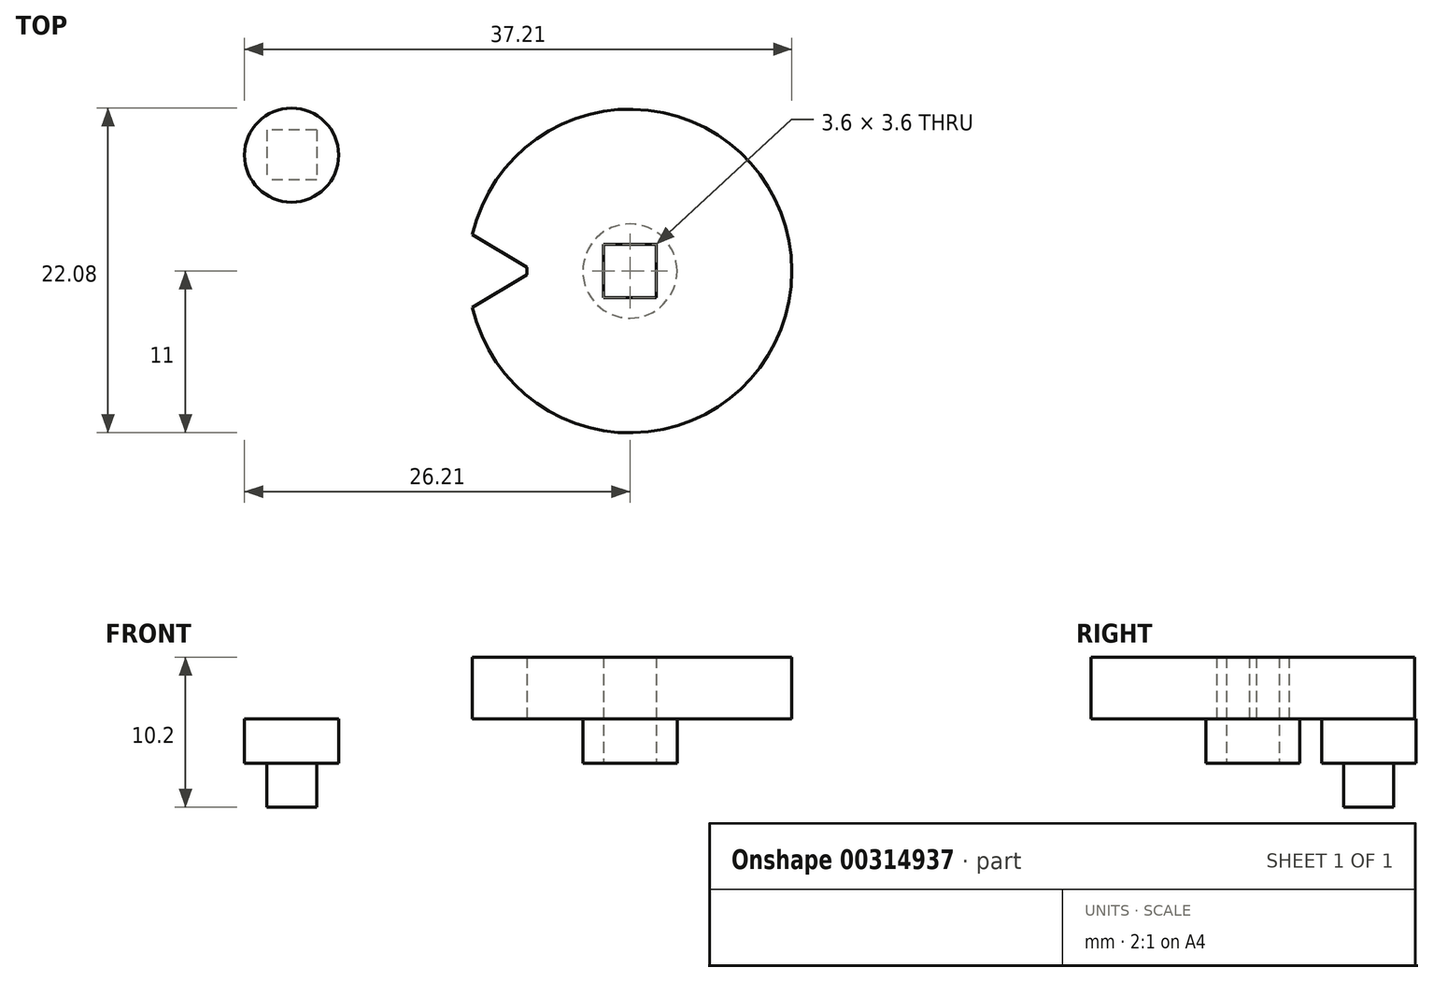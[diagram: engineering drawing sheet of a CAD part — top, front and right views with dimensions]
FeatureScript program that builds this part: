
annotation { "Feature Type Name" : "Feature", "Feature Type Description" : "" }
export const myFeature = defineFeature(function(context is Context, id is Id, definition is map)
    precondition{}
    {
        {
            var Q0;
            Q0=qCreatedBy(makeId("Top.planeOp"),FACE);
            var sketch = newSketch(context, id + "F0", { "sketchPlane" : qUnion([Q0])});
            skCircle(sketch, "E0", {"center": v(0, 0) * mm, "radius": 11 * mm});
            skSolve(sketch);
        }
        {
            var Q0;
            Q0 = qSketchRegion(id + "F0", true);
            extrude(context, id + "F1", {"entities" : qUnion([Q0]), "depth" : 4.2 * mm});
        }
        {
            var Q0;
            Q0=makeQuery(id+"F1.opExtrude","CAP_FACE",FACE,{"disambiguationData":[OSD([sQuery(id+"F0.wireOp",EDGE,"E0")])],"isStart":true});
            var sketch = newSketch(context, id + "F2", { "sketchPlane" : qUnion([Q0])});
            skLineSegment(sketch, "E1", {"start": v(0, 0) * mm, "end": v(-11, 0) * mm});
            skLineSegment(sketch, "E2", {"start": v(0, 0) * mm, "end": v(-7, -0.24) * mm});
            skLineSegment(sketch, "E3", {"start": v(0, 0) * mm, "end": v(-7, 0.24) * mm});
            skLineSegment(sketch, "E4", {"start": v(0, 0) * mm, "end": v(-10.72, -2.47) * mm});
            skLineSegment(sketch, "E5", {"start": v(0, 0) * mm, "end": v(-10.72, 2.47) * mm});
            skArc(sketch, "E6", {"start": v(-7, -0.24) * mm, "mid": v(-7, 0) * mm, "end": v(-7, 0.24) * mm});
            skArc(sketch, "E7", {"start": v(-10.72, -2.47) * mm, "mid": v(-11, 0) * mm, "end": v(-10.72, 2.47) * mm});
            skLineSegment(sketch, "E8", {"start": v(-10.72, -2.47) * mm, "end": v(-7, -0.24) * mm});
            skLineSegment(sketch, "E9", {"start": v(-7, 0.24) * mm, "end": v(-10.72, 2.47) * mm});
            skSolve(sketch);
        }
        {
            var Q0;
            {var subQ5=sQuery(id+"F2.wireOp",EDGE,"E8");Q0=makeQuery(id+"F2.imprint","IMPRINT",FACE,{"disambiguationData":[TD([[makeQuery(id+"F2.imprint","IMPRINT",EDGE,{"derivedFrom":subQ5}),1.0]])]});}
            var Q1;
            {var subQ5=sQuery(id+"F2.wireOp",EDGE,"E9");Q1=makeQuery(id+"F2.imprint","IMPRINT",FACE,{"disambiguationData":[TD([[makeQuery(id+"F2.imprint","IMPRINT",EDGE,{"derivedFrom":subQ5}),1.0]])]});}
            extrude(context, id + "F3", {"entities" : qUnion([Q0, Q1]), "operationType" : NewBodyOperationType.REMOVE, "endBound" : BoundingType.THROUGH_ALL, "oppositeDirection" : true, "depth" : 25 * mm});
        }
        {
            var Q0;
            Q0=qCreatedBy(makeId("Right.planeOp"),FACE);
            var sketch = newSketch(context, id + "F4", { "sketchPlane" : qUnion([Q0])});
            skLineSegment(sketch, "E10", {"start": v(0, 0) * mm, "end": v(0, -16.64) * mm});
            skSolve(sketch);
        }
        {
            var Q0;
            Q0=makeQuery(id+"F1.opExtrude","CAP_FACE",FACE,{"disambiguationData":[OSD([sQuery(id+"F0.wireOp",EDGE,"E0")])],"isStart":true});
            var sketch = newSketch(context, id + "F5", { "sketchPlane" : qUnion([Q0])});
            skCircle(sketch, "E11", {"center": v(0, 0) * mm, "radius": 3.2 * mm});
            skSolve(sketch);
        }
        {
            var Q0;
            Q0 = qSketchRegion(id + "F5", true);
            extrude(context, id + "F6", {"entities" : qUnion([Q0]), "operationType" : NewBodyOperationType.ADD, "depth" : 3 * mm});
        }
        {
            var Q0;
            Q0=makeQuery(id+"F6.opExtrude","CAP_FACE",FACE,{"disambiguationData":[OSD([sQuery(id+"F5.wireOp",EDGE,"E11")])],"isStart":false});
            var sketch = newSketch(context, id + "F7", { "sketchPlane" : qUnion([Q0])});
            skLineSegment(sketch, "E12.bottom", {"start": v(1.8, -1.8) * mm, "end": v(-1.8, -1.8) * mm});
            skLineSegment(sketch, "E12.top", {"start": v(1.8, 1.8) * mm, "end": v(-1.8, 1.8) * mm});
            skLineSegment(sketch, "E12.left", {"start": v(1.8, -1.8) * mm, "end": v(1.8, 1.8) * mm});
            skLineSegment(sketch, "E12.right", {"start": v(-1.8, -1.8) * mm, "end": v(-1.8, 1.8) * mm});
            skPoint(sketch, "E12.middle", {"position": v(0, 0) * mm});
            skSolve(sketch);
        }
        {
            var Q0;
            Q0 = qSketchRegion(id + "F7", true);
            extrude(context, id + "F8", {"entities" : qUnion([Q0]), "operationType" : NewBodyOperationType.REMOVE, "endBound" : BoundingType.THROUGH_ALL, "oppositeDirection" : true, "depth" : 25 * mm});
        }
        {
            var Q0;
            Q0=qCreatedBy(makeId("Top.planeOp"),FACE);
            var sketch = newSketch(context, id + "F9", { "sketchPlane" : qUnion([Q0])});
            skCircle(sketch, "E13", {"center": v(-23, 7.88) * mm, "radius": 3.2 * mm});
            skSolve(sketch);
        }
        {
            var Q0;
            Q0 = qSketchRegion(id + "F9", true);
            extrude(context, id + "F10", {"entities" : qUnion([Q0]), "oppositeDirection" : true, "depth" : 3 * mm});
        }
        {
            var Q0;
            Q0=makeQuery(id+"F10.opExtrude","CAP_FACE",FACE,{"disambiguationData":[OSD([sQuery(id+"F9.wireOp",EDGE,"E13")])],"isStart":false});
            var sketch = newSketch(context, id + "F11", { "sketchPlane" : qUnion([Q0])});
            skLineSegment(sketch, "E14.bottom", {"start": v(-21.3, -9.58) * mm, "end": v(-24.7, -9.58) * mm});
            skLineSegment(sketch, "E14.top", {"start": v(-21.3, -6.18) * mm, "end": v(-24.7, -6.18) * mm});
            skLineSegment(sketch, "E14.left", {"start": v(-21.3, -9.58) * mm, "end": v(-21.3, -6.18) * mm});
            skLineSegment(sketch, "E14.right", {"start": v(-24.7, -9.58) * mm, "end": v(-24.7, -6.18) * mm});
            skPoint(sketch, "E14.middle", {"position": v(-23, -7.88) * mm});
            skSolve(sketch);
        }
        {
            var Q0;
            Q0 = qSketchRegion(id + "F11", true);
            extrude(context, id + "F12", {"entities" : qUnion([Q0]), "operationType" : NewBodyOperationType.ADD, "depth" : 3 * mm});
        }
    });
